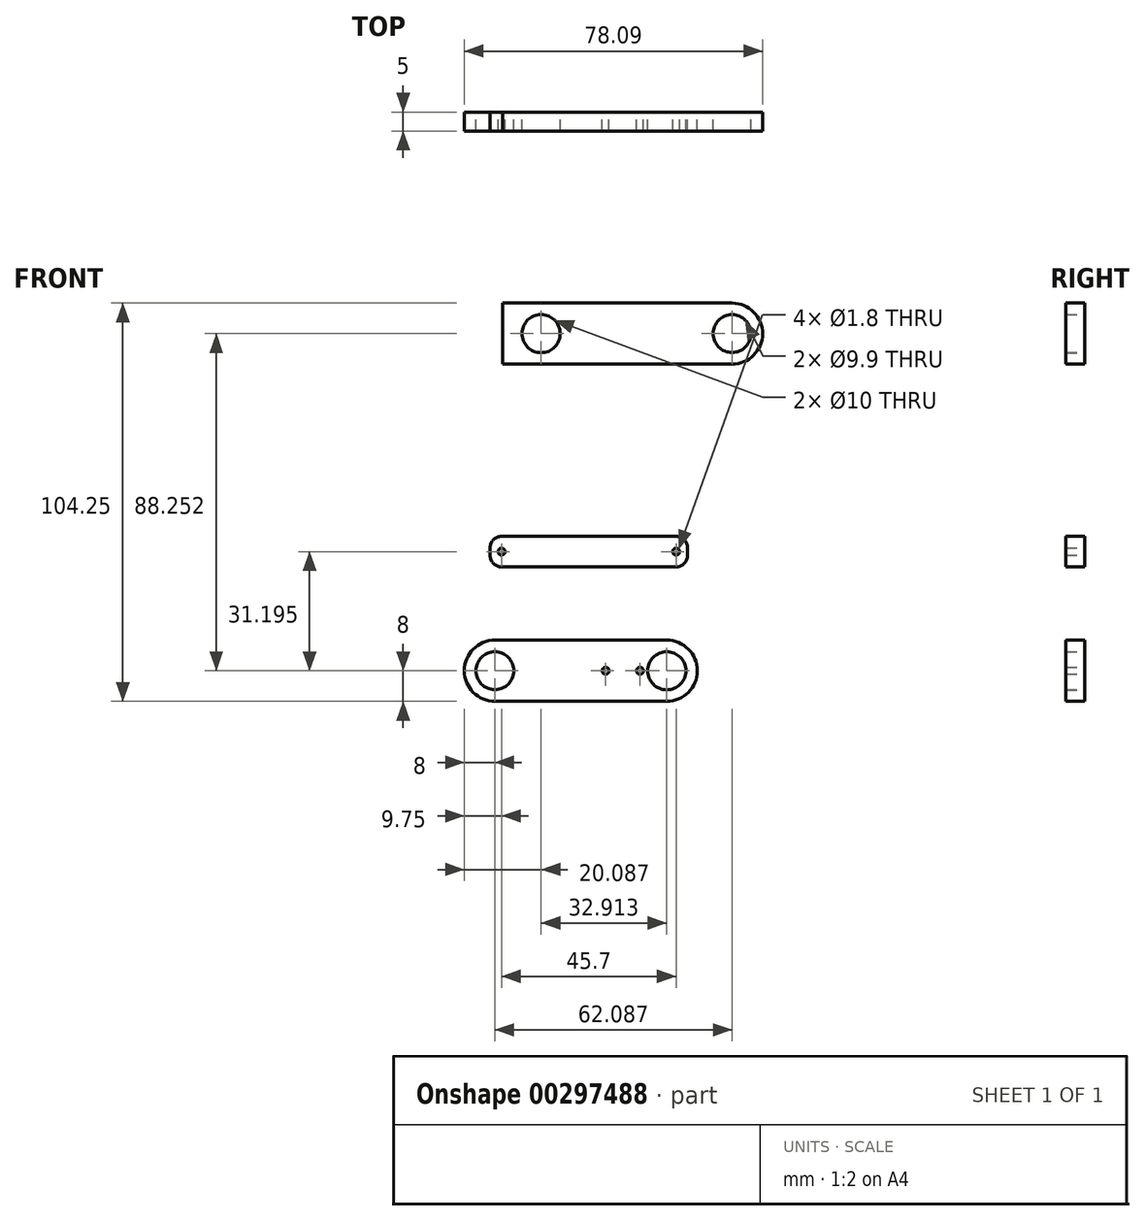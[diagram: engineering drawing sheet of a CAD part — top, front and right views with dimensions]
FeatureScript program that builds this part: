
annotation { "Feature Type Name" : "Feature", "Feature Type Description" : "" }
export const myFeature = defineFeature(function(context is Context, id is Id, definition is map)
    precondition{}
    {
        {
            var Q0;
            Q0=qCreatedBy(makeId("Front.planeOp"),FACE);
            var sketch = newSketch(context, id + "F0", { "sketchPlane" : qUnion([Q0])});
            skPoint(sketch, "E0", {"position": v(-74.78, 0) * mm});
            skPoint(sketch, "E1", {"position": v(0, 0) * mm});
            skPoint(sketch, "E2", {"position": v(0, -13) * mm});
            skPoint(sketch, "E3", {"position": v(40, -64) * mm});
            skPoint(sketch, "E4", {"position": v(-50, -13) * mm});
            skLineSegment(sketch, "E5", {"start": v(-50, -13) * mm, "end": v(0, -13) * mm});
            skLineSegment(sketch, "E6.bottom", {"start": v(37.49, 126.92) * mm, "end": v(-22.51, 126.92) * mm});
            skLineSegment(sketch, "E6.top", {"start": v(37.49, 142.92) * mm, "end": v(-22.51, 142.92) * mm});
            skLineSegment(sketch, "E6.left", {"start": v(45.49, 134.92) * mm, "end": v(45.49, 134.92) * mm});
            skPoint(sketch, "E6.middle", {"position": v(0, 134.92) * mm});
            skCircle(sketch, "E7", {"center": v(37.49, 134.92) * mm, "radius": 4.95 * mm});
            skPoint(sketch, "E7.centerSnap0", {"position": v(45.49, 134.92) * mm});
            skLineSegment(sketch, "E8.bottom", {"start": v(22.85, 73.87) * mm, "end": v(-22.85, 73.87) * mm});
            skLineSegment(sketch, "E8.top", {"start": v(22.85, 81.87) * mm, "end": v(-22.85, 81.87) * mm});
            skLineSegment(sketch, "E8.left", {"start": v(25.85, 76.87) * mm, "end": v(25.85, 78.87) * mm});
            skLineSegment(sketch, "E8.right", {"start": v(-25.85, 76.87) * mm, "end": v(-25.85, 78.87) * mm});
            skPoint(sketch, "E8.middle", {"position": v(0, 77.87) * mm});
            skLineSegment(sketch, "E9.bottom", {"start": v(20.4, 38.67) * mm, "end": v(-24.6, 38.67) * mm});
            skLineSegment(sketch, "E9.top", {"start": v(20.4, 54.67) * mm, "end": v(-24.6, 54.67) * mm});
            skLineSegment(sketch, "E9.right", {"start": v(-30.81, 41.63) * mm, "end": v(-30.81, 41.63) * mm});
            skPoint(sketch, "E9.middle", {"position": v(0, 46.67) * mm});
            skCircle(sketch, "E10", {"center": v(-22.85, 77.87) * mm, "radius": 0.9 * mm});
            skPoint(sketch, "E10.centerSnap0", {"position": v(-25.85, 77.87) * mm});
            skCircle(sketch, "E11", {"center": v(22.85, 77.87) * mm, "radius": 0.9 * mm});
            skPoint(sketch, "E11.centerSnap0", {"position": v(25.85, 77.87) * mm});
            skCircle(sketch, "E12", {"center": v(-24.6, 46.67) * mm, "radius": 4.95 * mm});
            skPoint(sketch, "E13", {"position": v(20.4, 46.67) * mm});
            skCircle(sketch, "E14.1.0", {"center": v(13.4, 46.67) * mm, "radius": 0.9 * mm});
            skCircle(sketch, "E14.1.1", {"center": v(4.4, 46.67) * mm, "radius": 0.9 * mm});
            skCircle(sketch, "E15", {"center": v(-12.51, 134.92) * mm, "radius": 5 * mm});
            skCircle(sketch, "E16", {"center": v(20.4, 46.67) * mm, "radius": 5 * mm});
            skPoint(sketch, "E17.visualSharp", {"position": v(45.49, 142.92) * mm});
            skArc(sketch, "E17.filletArc", {"start": v(45.49, 134.92) * mm, "mid": v(43.14, 140.58) * mm, "end": v(37.49, 142.92) * mm});
            skPoint(sketch, "E18.visualSharp", {"position": v(45.49, 126.92) * mm});
            skArc(sketch, "E18.filletArc", {"start": v(37.49, 126.92) * mm, "mid": v(43.14, 129.27) * mm, "end": v(45.49, 134.92) * mm});
            skPoint(sketch, "E19.visualSharp", {"position": v(-25.85, 81.87) * mm});
            skArc(sketch, "E19.filletArc", {"start": v(-22.85, 81.87) * mm, "mid": v(-24.97, 80.99) * mm, "end": v(-25.85, 78.87) * mm});
            skPoint(sketch, "E20.visualSharp", {"position": v(-25.85, 73.87) * mm});
            skArc(sketch, "E20.filletArc", {"start": v(-25.85, 76.87) * mm, "mid": v(-24.97, 74.74) * mm, "end": v(-22.85, 73.87) * mm});
            skPoint(sketch, "E21.visualSharp", {"position": v(25.85, 73.87) * mm});
            skArc(sketch, "E21.filletArc", {"start": v(22.85, 73.87) * mm, "mid": v(24.97, 74.74) * mm, "end": v(25.85, 76.87) * mm});
            skPoint(sketch, "E22.visualSharp", {"position": v(25.85, 81.87) * mm});
            skArc(sketch, "E22.filletArc", {"start": v(25.85, 78.87) * mm, "mid": v(24.97, 80.99) * mm, "end": v(22.85, 81.87) * mm});
            skPoint(sketch, "E23.visualSharp", {"position": v(-41.4, 54.67) * mm});
            skArc(sketch, "E23.filletArc", {"start": v(-24.6, 54.67) * mm, "mid": v(-31.82, 50.1) * mm, "end": v(-30.81, 41.63) * mm});
            skPoint(sketch, "E24.visualSharp", {"position": v(-28.4, 38.67) * mm});
            skArc(sketch, "E24.filletArc", {"start": v(-30.81, 41.63) * mm, "mid": v(-28.04, 39.45) * mm, "end": v(-24.6, 38.67) * mm});
            skArc(sketch, "E25.filletArc", {"start": v(28.4, 46.67) * mm, "mid": v(26.06, 52.33) * mm, "end": v(20.4, 54.67) * mm});
            skPoint(sketch, "E26.visualSharp", {"position": v(41.4, 38.67) * mm});
            skArc(sketch, "E26.filletArc", {"start": v(20.4, 38.67) * mm, "mid": v(26.06, 41.01) * mm, "end": v(28.4, 46.67) * mm});
            skLineSegment(sketch, "E27", {"start": v(-22.51, 142.92) * mm, "end": v(-22.51, 126.92) * mm});
            skLineSegment(sketch, "E28.bottom", {"start": v(7.49, 142.92) * mm, "end": v(-52.51, 142.92) * mm});
            skLineSegment(sketch, "E28.top", {"start": v(7.49, 147.92) * mm, "end": v(-52.51, 147.92) * mm});
            skLineSegment(sketch, "E28.left", {"start": v(7.49, 142.92) * mm, "end": v(7.49, 147.92) * mm});
            skLineSegment(sketch, "E28.right", {"start": v(-52.51, 142.92) * mm, "end": v(-52.51, 147.92) * mm});
            skLineSegment(sketch, "E29.bottom", {"start": v(-22.51, 126.92) * mm, "end": v(-27.51, 126.92) * mm});
            skLineSegment(sketch, "E29.top", {"start": v(-22.51, 142.92) * mm, "end": v(-27.51, 142.92) * mm});
            skLineSegment(sketch, "E29.left", {"start": v(-22.51, 126.92) * mm, "end": v(-22.51, 142.92) * mm});
            skLineSegment(sketch, "E29.right", {"start": v(-27.51, 126.92) * mm, "end": v(-27.51, 142.92) * mm});
            skLineSegment(sketch, "E30.bottom", {"start": v(-3, 0) * mm, "end": v(27.75, 0) * mm});
            skLineSegment(sketch, "E30.left", {"start": v(-3, 0) * mm, "end": v(-3, -69.5) * mm});
            skPoint(sketch, "E31", {"position": v(40, -69.5) * mm});
            skCircle(sketch, "E32", {"center": v(16, -64.5) * mm, "radius": 1.4 * mm});
            skCircle(sketch, "E33", {"center": v(64, -64.5) * mm, "radius": 1.4 * mm});
            skLineSegment(sketch, "E34", {"start": v(-3, -69.5) * mm, "end": v(17.5, -69.5) * mm});
            skLineSegment(sketch, "E35.trimOffspring", {"start": v(62.5, -69.5) * mm, "end": v(66.5, -69.5) * mm});
            skLineSegment(sketch, "E36.top", {"start": v(19.5, -58.5) * mm, "end": v(60.5, -58.5) * mm});
            skLineSegment(sketch, "E36.left", {"start": v(19.5, -67.5) * mm, "end": v(19.5, -58.5) * mm});
            skLineSegment(sketch, "E36.right", {"start": v(60.5, -67.5) * mm, "end": v(60.5, -58.5) * mm});
            skLineSegment(sketch, "E37", {"start": v(68.5, 0) * mm, "end": v(68.5, -67.5) * mm});
            skPoint(sketch, "E38.visualSharp", {"position": v(19.5, -69.5) * mm});
            skArc(sketch, "E38.filletArc", {"start": v(17.5, -69.5) * mm, "mid": v(18.91, -68.91) * mm, "end": v(19.5, -67.5) * mm});
            skPoint(sketch, "E39.visualSharp", {"position": v(60.5, -69.5) * mm});
            skArc(sketch, "E39.filletArc", {"start": v(60.5, -67.5) * mm, "mid": v(61.09, -68.91) * mm, "end": v(62.5, -69.5) * mm});
            skPoint(sketch, "E40.visualSharp", {"position": v(68.5, -69.5) * mm});
            skArc(sketch, "E40.filletArc", {"start": v(66.5, -69.5) * mm, "mid": v(67.91, -68.91) * mm, "end": v(68.5, -67.5) * mm});
            skPoint(sketch, "E41", {"position": v(40, -58.5) * mm});
            skCircle(sketch, "E42", {"center": v(0, -13) * mm, "radius": 0.9 * mm});
            skPoint(sketch, "E43.start.orphan", {"position": v(-35, -13) * mm});
            skPoint(sketch, "E44", {"position": v(32.75, 0) * mm});
            skLineSegment(sketch, "E45.top", {"start": v(37.75, 5) * mm, "end": v(27.75, 5) * mm});
            skLineSegment(sketch, "E45.left", {"start": v(37.75, 0) * mm, "end": v(37.75, 5) * mm});
            skLineSegment(sketch, "E45.right", {"start": v(27.75, 0) * mm, "end": v(27.75, 5) * mm});
            skLineSegment(sketch, "E46.trimOffspring", {"start": v(37.75, 0) * mm, "end": v(68.5, 0) * mm});
            skSolve(sketch);
        }
        {
            var Q0;
            Q0=makeQuery(id+"F0.imprint","IMPRINT",FACE,{"disambiguationData":[TD([[makeQuery(id+"F0.imprint","IMPRINT",EDGE,{"derivedFrom":sQuery(id+"F0.wireOp",EDGE,"E6.bottom")}),-1.0]])]});
            var Q1;
            Q1=makeQuery(id+"F0.imprint","IMPRINT",FACE,{"disambiguationData":[TD([[makeQuery(id+"F0.imprint","IMPRINT",EDGE,{"derivedFrom":sQuery(id+"F0.wireOp",EDGE,"E8.bottom")}),-1.0]])]});
            var Q2;
            Q2=makeQuery(id+"F0.imprint","IMPRINT",FACE,{"disambiguationData":[TD([[makeQuery(id+"F0.imprint","IMPRINT",EDGE,{"derivedFrom":sQuery(id+"F0.wireOp",EDGE,"E9.bottom")}),-1.0]])]});
            extrude(context, id + "F1", {"entities" : qUnion([Q0, Q1, Q2]), "depth" : 5 * mm});
        }
    });
